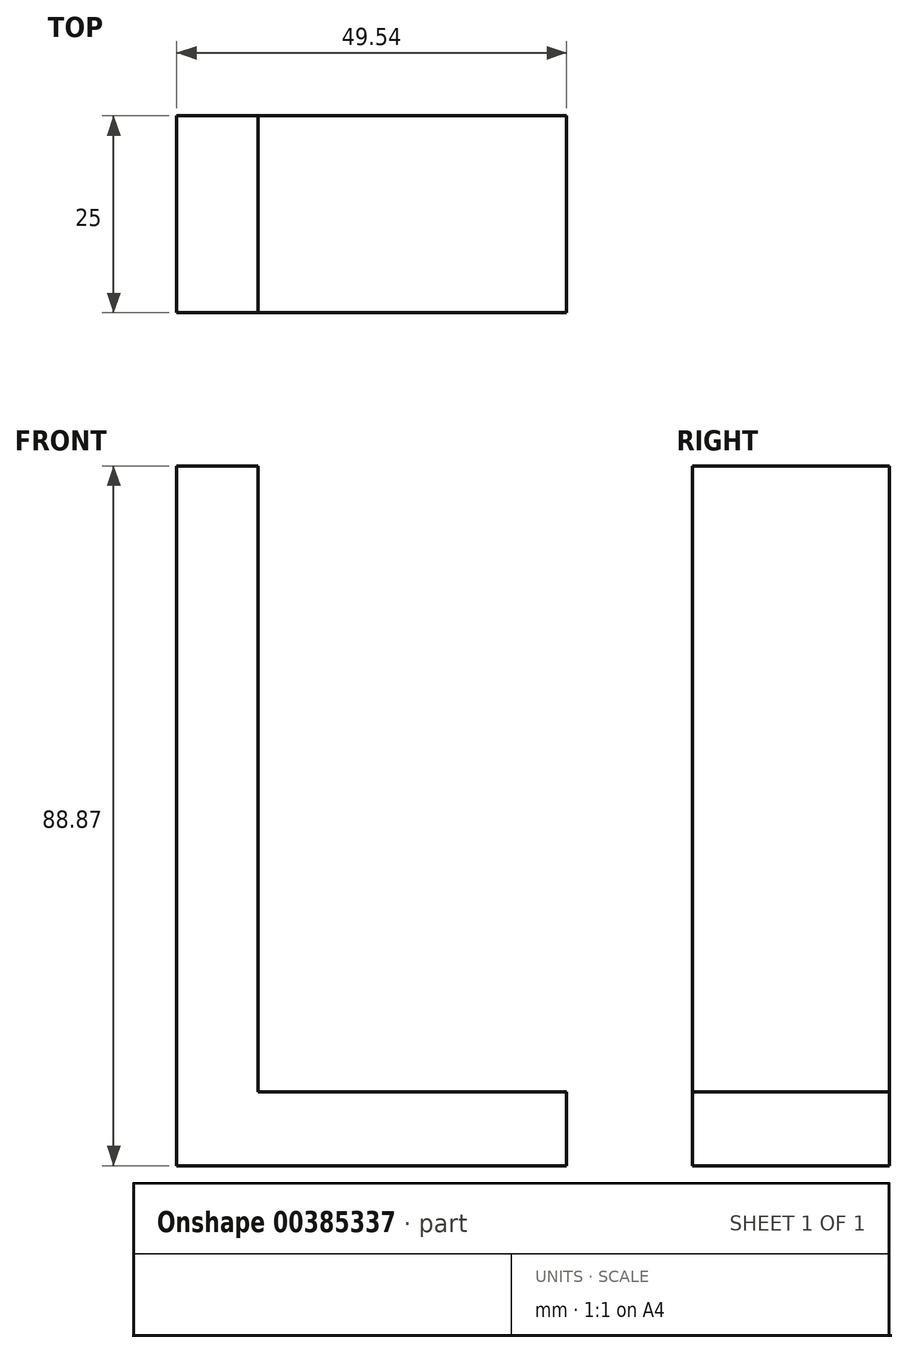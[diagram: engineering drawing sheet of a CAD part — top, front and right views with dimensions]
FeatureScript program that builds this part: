
annotation { "Feature Type Name" : "Feature", "Feature Type Description" : "" }
export const myFeature = defineFeature(function(context is Context, id is Id, definition is map)
    precondition{}
    {
        {
            var Q0;
            Q0=qCreatedBy(makeId("Front.planeOp"),FACE);
            var sketch = newSketch(context, id + "F0", { "sketchPlane" : qUnion([Q0])});
            skText(sketch, "E0", { "text": "L", "fontName": "OpenSans-Regular.ttf"});
            const initialGuessF0  = {"E0": [-0.05473, -0.04828, 1, 0, 0.08963]};
            skSetInitialGuess(sketch, initialGuessF0);
            skSolve(sketch);
        }
        {
            var Q0;
            Q0 = qSketchRegion(id + "F0", true);
            extrude(context, id + "F1", {"entities" : qUnion([Q0]), "depth" : 25 * mm});
        }
    });
